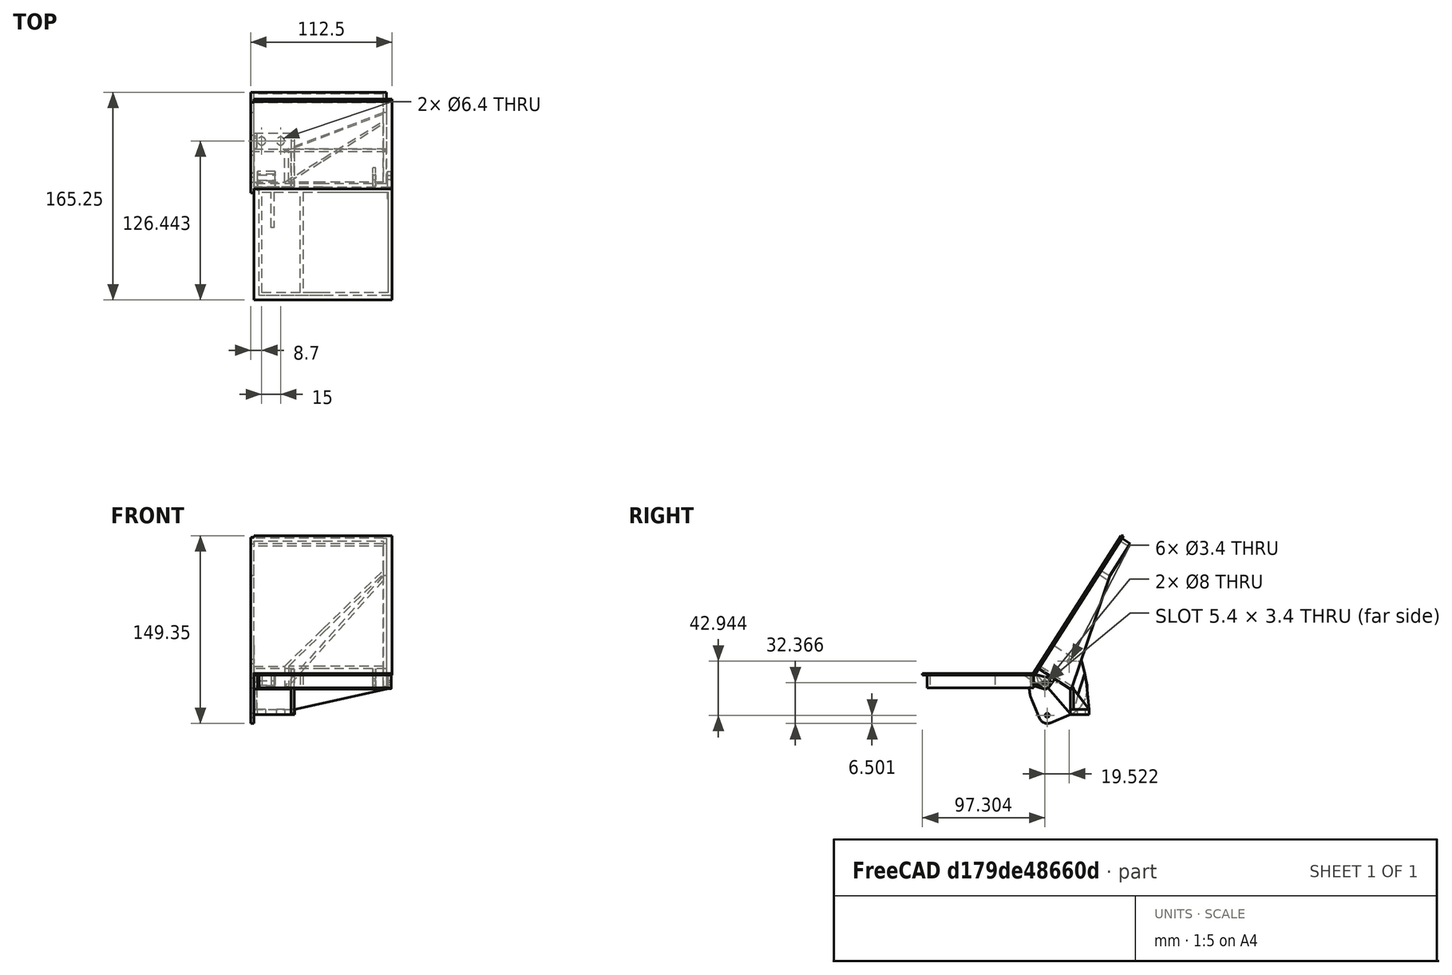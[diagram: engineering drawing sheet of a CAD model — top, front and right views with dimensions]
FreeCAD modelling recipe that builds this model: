
FCSTD DOCUMENT  (FreeCAD 0.19R24291 (Git))
Label: Hopper 6
License: All rights reserved
LicenseURL: http://en.wikipedia.org/wiki/All_rights_reserved
objects: Sketcher::SketchObject×20, PartDesign::Pad×16, PartDesign::Pocket×5, PartDesign::Mirrored×2, PartDesign::Body×2, PartDesign::SubShapeBinder×1, Spreadsheet::Sheet×1
note: 67 computed .brp shape members not serialized (recipe doc carries the construction recipe); baked Part::Feature solids carry a one-line shape summary decoded from their .brp

FEATURE [Sketcher::SketchObject] Sketch
  AttachmentOffset = pos=(0,0,0) rot=(1,0,0;1.00409rad)
  FullyConstrained = true
  MapMode = 5
  Placement = pos=(0,0,0) rot=(1,0,0;1.00409rad)
  Support = -> [XY_Plane]
  expr: .AttachmentOffset.Rotation.Angle = Spreadsheet.BackAngle
  sketch-geometry (4):
    g0: LineSegment StartX=0 StartY=0 StartZ=0 EndX=55 EndY=0 EndZ=0
    g1: LineSegment StartX=55 StartY=0 StartZ=0 EndX=55 EndY=130 EndZ=0
    g2: LineSegment StartX=55 StartY=130 StartZ=0 EndX=0 EndY=130 EndZ=0
    g3: LineSegment StartX=0 StartY=130 StartZ=0 EndX=0 EndY=0 EndZ=0
  constraints (11):
    c: Coincident(g0,g1)
    c: Coincident(g1,g2)
    c: Coincident(g2,g3)
    c: Coincident(g3,g0)
    c: Horizontal(g0)
    c: Horizontal(g2)
    c: Vertical(g1)
    c: Vertical(g3)
    c: Coincident(g0,g-1)
    c: Distance(g1) = 130
    c: Distance(g0) = 55
FEATURE [PartDesign::Pad] Pad
  Direction = (0,-1,0)
  Length = 1.5
  Length2 = 100
  Profile = -> Sketch
  Type = 0
  UseCustomVector = true
FEATURE [PartDesign::Mirrored] Mirrored
  BaseFeature = -> Pad
  MirrorPlane = -> Sketch [V_Axis]
  Originals = -> [Pad]
FEATURE [Sketcher::SketchObject] Sketch001
  FullyConstrained = true
  MapMode = 5
  Placement = pos=(-55,0,0) rot=(0.57735,-0.57735,-0.57735;2.0944rad)
  Support = -> [Mirrored]
  expr: Constraints[34] = 10.33mm
  expr: Constraints[41] = Spreadsheet.BackAngle
  sketch-geometry (23):
    g0: ArcOfCircle CenterX=-24.9137 CenterY=5.10111 CenterZ=0 NormalX=0 NormalY=0 NormalZ=1 AngleXU=0 Radius=12.5 StartAngle=0.484009 EndAngle=3.43434
    g1: ArcOfCircle CenterX=-9.25499 CenterY=-33.1694 CenterZ=0 NormalX=0 NormalY=0 NormalZ=1 AngleXU=0 Radius=6.5 StartAngle=3.35841 EndAngle=6.84312
    g2: Circle CenterX=-7.30441 CenterY=-7.30441 CenterZ=0 NormalX=0 NormalY=0 NormalZ=1 AngleXU=0 Radius=4
    g3: Circle CenterX=-9.25499 CenterY=-33.1694 CenterZ=0 NormalX=0 NormalY=0 NormalZ=1 AngleXU=0 Radius=1.7
    g4: Circle CenterX=-26.826 CenterY=9.77502 CenterZ=0 NormalX=0 NormalY=0 NormalZ=1 AngleXU=0 Radius=1.7
    g5: LineSegment StartX=-9.25499 StartY=-33.1694 StartZ=0 EndX=-18.0405 EndY=-11.6972 EndZ=0
    g6: LineSegment StartX=-18.0405 StartY=-11.6972 StartZ=0 EndX=-26.826 EndY=9.77502 EndZ=0
    g7: LineSegment StartX=-18.0405 StartY=-11.6972 StartZ=0 EndX=-7.30441 EndY=-7.30441 EndZ=0
    g8: GeomPoint X=-29.6472 Y=16.6702 Z=0
    g9: ArcOfCircle CenterX=-18.0405 CenterY=-11.6972 CenterZ=0 NormalX=0 NormalY=0 NormalZ=1 AngleXU=0 Radius=23 StartAngle=2.53079 EndAngle=4.81858
    g10: ArcOfCircle CenterX=-18.0405 CenterY=-11.6972 CenterZ=0 NormalX=0 NormalY=0 NormalZ=1 AngleXU=0 Radius=23 StartAngle=5.38296 EndAngle=7.67074
    g11: LineSegment StartX=-7.30441 StartY=-7.30441 StartZ=0 EndX=-7.30441 EndY=0 EndZ=0
    g12: LineSegment StartX=-7.30441 StartY=-7.30441 StartZ=0 EndX=0 EndY=-7.30441 EndZ=0
    g13: ArcOfCircle CenterX=-18.0405 CenterY=-11.6972 CenterZ=0 NormalX=0 NormalY=0 NormalZ=1 AngleXU=0 Radius=23 StartAngle=5.38296 EndAngle=6.84989
    g14: LineSegment StartX=-28.0362 StartY=46.853 StartZ=0 EndX=1.36396 EndY=0.650563 EndZ=0
    g15: LineSegment StartX=0 StartY=0 StartZ=0 EndX=1.26551 EndY=0.805287 EndZ=0
    g16: LineSegment StartX=1.26551 StartY=0.805287 StartZ=0 EndX=1.36396 EndY=0.650563 EndZ=0
    g17: ArcOfCircle CenterX=-18.0405 CenterY=-11.6972 CenterZ=0 NormalX=0 NormalY=0 NormalZ=1 AngleXU=0 Radius=23 StartAngle=2.91307 EndAngle=4.32118
    g18: ArcOfCircle CenterX=-9.25499 CenterY=-33.1694 CenterZ=0 NormalX=0 NormalY=0 NormalZ=1 AngleXU=0 Radius=6.5 StartAngle=4.32118 EndAngle=5.88035
    g19: ArcOfCircle CenterX=-18.0405 CenterY=-11.6972 CenterZ=0 NormalX=0 NormalY=0 NormalZ=1 AngleXU=0 Radius=23 StartAngle=5.88035 EndAngle=6.84989
    g20: LineSegment StartX=-11.7335 StartY=-39.1783 StartZ=0 EndX=-26.8105 EndY=-32.9595 EndZ=0
    g21: LineSegment StartX=-3.2753 StartY=-35.7176 StartZ=0 EndX=3.11842 EndY=-20.7138 EndZ=0
    g22: LineSegment StartX=-40.4425 StartY=-6.48667 StartZ=0 EndX=-28.0362 EndY=46.853 EndZ=0
  constraints (66):
    c: Coincident(g3,g1)
    c: Coincident(g5,g1)
    c: Coincident(g6,g5)
    c: Coincident(g6,g4)
    c: Coincident(g7,g5)
    c: Coincident(g7,g2)
    c: Distance(g7) = 11.6
    c: Distance(g1,g4) = 46.4
    c: Perpendicular(g6,g7)
    c: Perpendicular(g5,g7)
    c: PointOnObject(g0,g6)
    c: Diameter(g0) = 25
    c: PointOnObject(g8,g0)
    c: PointOnObject(g8,g6)
    c: Distance(g4,g8) = 7.45
    c: Equal(g6,g5)
    c: Diameter(g1) = 13
    c: Coincident(g9,g5)
    c: Coincident(g9,g0)
    c: Coincident(g10,g9)
    c: Coincident(g10,g0)
    c: Equal(g9,g10)
    c: Diameter(g10) = 46
    c: Coincident(g9,g1)
    c: Diameter(g2) = 8
    c: Diameter(g3) = 3.4
    c: Equal(g3,g4)
    c: Coincident(g11,g2)
    c: PointOnObject(g11,g-1)
    c: Vertical(g11)
    c: Coincident(g12,g2)
    c: PointOnObject(g12,g-2)
    c: Horizontal(g12)
    c: Equal(g12,g11)
    c: Distance(g2,g-1) = 10.33
    c: Distance(g12) = 7.30441
    c: Coincident(g10,g1)
    c: Coincident(g13,g9)
    c: Coincident(g13,g1)
    c: Coincident(g14,g13)
    c: Tangent(g14,g10)
    c: Angle(g14,g-1) = 1.00409
    c: Coincident(g15,g-1)
    c: Distance(g15) = 1.5
    c: Coincident(g16,g15)
    c: Perpendicular(g15,g16)
    c: Coincident(g13,g16)
    c: Coincident(g17,g5)
    c: PointOnObject(g17,g9)
    c: Coincident(g18,g3)
    c: PointOnObject(g18,g1)
    c: Coincident(g19,g17)
    c: Coincident(g19,g14)
    c: Coincident(g20,g18)
    c: Coincident(g20,g17)
    c: Coincident(g21,g18)
    c: Coincident(g21,g19)
    c: Tangent(g17,g20)
    c: Tangent(g20,g18)
    c: Tangent(g18,g21)
    c: Tangent(g21,g19)
    c: Coincident(g22,g17)
    c: Coincident(g22,g14)
    c: Tangent(g22,g17)
    c: Tangent(g22,g0)
    c: Perpendicular(g14,g15)
FEATURE [PartDesign::Pad] Pad001
  BaseFeature = -> Mirrored
  Direction = (1,1,1)
  Length = 1.5
  Length2 = 100
  Profile = -> Sketch001
  Type = 0
FEATURE [Sketcher::SketchObject] Sketch002
  FullyConstrained = false
  MapMode = 5
  Placement = pos=(0,-9e-15,5.7e-15) rot=(0,0.876601,0.481218;3.14159rad)
  Support = -> [Pad001]
  sketch-geometry (13):
    g0: LineSegment StartX=-50.3995 StartY=127.591 StartZ=0 EndX=-50.3995 EndY=4.62451 EndZ=0
    g1: LineSegment StartX=55.0842 StartY=7.02451 StartZ=0 EndX=30.5525 EndY=7.02451 EndZ=0
    g2: LineSegment StartX=30.5525 StartY=7.02451 StartZ=0 EndX=-47.9995 EndY=97.2605 EndZ=0
    g3: LineSegment StartX=-47.9995 StartY=97.2605 StartZ=0 EndX=-47.9995 EndY=127.591 EndZ=0
    g4: LineSegment StartX=-47.9995 StartY=127.591 StartZ=0 EndX=-50.3995 EndY=127.591 EndZ=0
    g5: LineSegment StartX=-50.3995 StartY=4.62451 StartZ=0 EndX=55.0842 EndY=4.62451 EndZ=0
    g6: LineSegment StartX=55.0842 StartY=4.62451 StartZ=0 EndX=55.0842 EndY=7.02451 EndZ=0
    g7: LineSegment StartX=27.3705 StartY=7.02451 StartZ=0 EndX=-47.9995 EndY=93.6052 EndZ=0
    g8: LineSegment StartX=-47.9995 StartY=93.6052 StartZ=0 EndX=-47.9995 EndY=7.02451 EndZ=0
    g9: LineSegment StartX=-47.9995 StartY=7.02451 StartZ=0 EndX=27.3705 EndY=7.02451 EndZ=0
    g10: LineSegment StartX=27.3705 StartY=7.02451 StartZ=0 EndX=27.3705 EndY=4.62451 EndZ=0
    g11: LineSegment StartX=-47.9995 StartY=93.6052 StartZ=0 EndX=-50.3995 EndY=93.6052 EndZ=0
    g12: LineSegment StartX=-27.7414 StartY=70.3339 StartZ=0 EndX=-25.9312 EndY=71.9097 EndZ=0
  constraints (37):
    c: Vertical(g0)
    c: Horizontal(g1)
    c: Coincident(g1,g2)
    c: Coincident(g2,g3)
    c: Coincident(g3,g4)
    c: Horizontal(g4)
    c: Horizontal(g5)
    c: Coincident(g5,g6)
    c: Coincident(g6,g1)
    c: Coincident(g7,g8)
    c: Vertical(g8)
    c: Coincident(g8,g9)
    c: Coincident(g9,g7)
    c: Horizontal(g9)
    c: Vertical(g6)
    c: Distance(g6) = 2.4
    c: Coincident(g10,g7)
    c: PointOnObject(g10,g5)
    c: Vertical(g10)
    c: Coincident(g11,g7)
    c: Horizontal(g11)
    c: Equal(g6,g10)
    c: Equal(g11,g4)
    c: Parallel(g7,g2)
    c: Coincident(g0,g5)
    c: Coincident(g0,g4)
    c: Vertical(g3)
    c: PointOnObject(g11,g0)
    c: Equal(g4,g6)
    c: PointOnObject(g12,g7)
    c: PointOnObject(g12,g2)
    c: Perpendicular(g2,g12)
    c: Equal(g6,g12)
    c: DistanceX(g7) = -47.9995
    c: DistanceY(g7) = 93.6052
    c: DistanceX(g5) = 55.0842
    c: DistanceY(g5) = 4.62451
FEATURE [PartDesign::Pad] Pad002
  BaseFeature = -> Pad001
  Direction = (1,1,1)
  Length = 30
  Length2 = 100
  Profile = -> Sketch002
  Type = 0
FEATURE [Sketcher::SketchObject] Sketch003
  FullyConstrained = true
  MapMode = 5
  Placement = pos=(-56.5,0,0) rot=(0.57735,-0.57735,-0.57735;2.0944rad)
  Support = -> [Pad002]
  expr: Constraints[6] = Sketch001.Constraints[6]
  expr: Constraints[7] = Sketch001.Constraints[7]
  expr: Constraints[11] = Sketch001.Constraints[11]
  expr: Constraints[14] = Sketch001.Constraints[14]
  expr: Constraints[22] = Sketch001.Constraints[22]
  expr: Constraints[41] = Sketch001.Constraints[41]
  expr: Constraints[16] = Sketch001.Constraints[16]
  expr: Constraints[44] = Sketch001.Constraints[44]
  expr: Constraints[24] = Sketch001.Constraints[24]
  expr: Constraints[25] = Sketch001.Constraints[25]
  expr: Constraints[34] = Sketch001.Constraints[34]
  expr: Constraints[43] = Sketch001.Constraints[43]
  sketch-geometry (31):
    g0: ArcOfCircle CenterX=-25.2764 CenterY=4.56949 CenterZ=0 NormalX=0 NormalY=0 NormalZ=1 AngleXU=0 Radius=12.5 StartAngle=0.51389 EndAngle=3.46422
    g1: ArcOfCircle CenterX=-8.48139 CenterY=-33.2161 CenterZ=0 NormalX=0 NormalY=0 NormalZ=1 AngleXU=0 Radius=6.5 StartAngle=3.38829 EndAngle=6.873
    g2: Circle CenterX=-7.30441 CenterY=-7.30441 CenterZ=0 NormalX=0 NormalY=0 NormalZ=1 AngleXU=0 Radius=4
    g3: Circle CenterX=-8.48139 CenterY=-33.2161 CenterZ=0 NormalX=0 NormalY=0 NormalZ=1 AngleXU=0 Radius=1.7
    g4: Circle CenterX=-27.3276 CenterY=9.18417 CenterZ=0 NormalX=0 NormalY=0 NormalZ=1 AngleXU=0 Radius=1.7
    g5: LineSegment StartX=-8.48139 StartY=-33.2161 StartZ=0 EndX=-17.9045 EndY=-12.016 EndZ=0
    g6: LineSegment StartX=-17.9045 StartY=-12.016 StartZ=0 EndX=-27.3276 EndY=9.18417 EndZ=0
    g7: LineSegment StartX=-17.9045 StartY=-12.016 StartZ=0 EndX=-7.30441 EndY=-7.30441 EndZ=0
    g8: GeomPoint X=-30.3535 Y=15.992 Z=0
    g9: ArcOfCircle CenterX=-17.9045 CenterY=-12.016 CenterZ=0 NormalX=0 NormalY=0 NormalZ=1 AngleXU=0 Radius=23 StartAngle=2.56067 EndAngle=4.84846
    g10: ArcOfCircle CenterX=-17.9045 CenterY=-12.016 CenterZ=0 NormalX=0 NormalY=0 NormalZ=1 AngleXU=0 Radius=23 StartAngle=5.41284 EndAngle=7.70062
    g11: LineSegment StartX=-7.30441 StartY=-7.30441 StartZ=0 EndX=-7.30441 EndY=0 EndZ=0
    g12: LineSegment StartX=-7.30441 StartY=-7.30441 StartZ=0 EndX=0 EndY=-7.30441 EndZ=0
    g13: ArcOfCircle CenterX=-17.9045 CenterY=-12.016 CenterZ=0 NormalX=0 NormalY=0 NormalZ=1 AngleXU=0 Radius=23 StartAngle=5.41284 EndAngle=6.84989
    g14: LineSegment StartX=-29.176 StartY=48.5391 StartZ=0 EndX=1.5 EndY=0.331766 EndZ=0
    g15: LineSegment StartX=0 StartY=0 StartZ=0 EndX=1.5 EndY=0 EndZ=0
    g16: LineSegment StartX=1.5 StartY=0 StartZ=0 EndX=1.5 EndY=0.331766 EndZ=0
    g17: ArcOfCircle CenterX=-17.9045 CenterY=-12.016 CenterZ=0 NormalX=0 NormalY=0 NormalZ=1 AngleXU=0 Radius=23 StartAngle=2.94295 EndAngle=4.35106
    g18: ArcOfCircle CenterX=-8.48139 CenterY=-33.2161 CenterZ=0 NormalX=0 NormalY=0 NormalZ=1 AngleXU=0 Radius=6.5 StartAngle=4.35106 EndAngle=5.91023
    g19: ArcOfCircle CenterX=-17.9045 CenterY=-12.016 CenterZ=0 NormalX=0 NormalY=0 NormalZ=1 AngleXU=0 Radius=23 StartAngle=5.91023 EndAngle=6.84989
    g20: LineSegment StartX=-10.7792 StartY=-39.2964 StartZ=0 EndX=-26.0353 EndY=-33.5308 EndZ=0
    g21: LineSegment StartX=-2.42824 StartY=-35.5845 StartZ=0 EndX=3.51436 EndY=-20.3965 EndZ=0
    g22: LineSegment StartX=-40.4522 StartY=-7.47706 StartZ=0 EndX=-29.176 EndY=48.5391 EndZ=0
    g23: ArcOfCircle CenterX=-17.9045 CenterY=-12.016 CenterZ=0 NormalX=0 NormalY=0 NormalZ=1 AngleXU=0 Radius=22.2 StartAngle=5.41284 EndAngle=7.70062
    g24: ArcOfCircle CenterX=-17.9045 CenterY=-12.016 CenterZ=0 NormalX=0 NormalY=0 NormalZ=1 AngleXU=0 Radius=22.2 StartAngle=2.56067 EndAngle=4.84846
    g25: ArcOfCircle CenterX=-3.07962 CenterY=-29.6007 CenterZ=0 NormalX=0 NormalY=0 NormalZ=1 AngleXU=0 Radius=0.8 StartAngle=2.27123 EndAngle=3.73142
    g26: ArcOfCircle CenterX=-14.7846 CenterY=-34.8034 CenterZ=0 NormalX=0 NormalY=0 NormalZ=1 AngleXU=0 Radius=0.8 StartAngle=0.246691 EndAngle=1.70686
    g27: ArcOfCircle CenterX=-8.48139 CenterY=-33.2161 CenterZ=0 NormalX=0 NormalY=0 NormalZ=1 AngleXU=0 Radius=5.7 StartAngle=3.38829 EndAngle=6.873
    g28: ArcOfCircle CenterX=-37.1315 CenterY=0.606294 CenterZ=0 NormalX=0 NormalY=0 NormalZ=1 AngleXU=0 Radius=0.8 StartAngle=5.70226 EndAngle=6.60581
    g29: ArcOfCircle CenterX=-14.3909 CenterY=10.7141 CenterZ=0 NormalX=0 NormalY=0 NormalZ=1 AngleXU=0 Radius=0.8 StartAngle=3.65547 EndAngle=4.55903
    g30: ArcOfCircle CenterX=-25.2764 CenterY=4.56949 CenterZ=0 NormalX=0 NormalY=0 NormalZ=1 AngleXU=0 Radius=11.7 StartAngle=0.51389 EndAngle=3.46422
  constraints (90):
    c: Coincident(g3,g1)
    c: Coincident(g5,g1)
    c: Coincident(g6,g5)
    c: Coincident(g6,g4)
    c: Coincident(g7,g5)
    c: Coincident(g7,g2)
    c: Distance(g7) = 11.6
    c: Distance(g1,g4) = 46.4
    c: Perpendicular(g6,g7)
    c: Perpendicular(g5,g7)
    c: PointOnObject(g0,g6)
    c: Diameter(g0) = 25
    c: PointOnObject(g8,g0)
    c: PointOnObject(g8,g6)
    c: Distance(g4,g8) = 7.45
    c: Equal(g6,g5)
    c: Diameter(g1) = 13
    c: Coincident(g9,g5)
    c: Coincident(g9,g0)
    c: Coincident(g10,g9)
    c: Coincident(g10,g0)
    c: Equal(g9,g10)
    c: Diameter(g10) = 46
    c: Coincident(g9,g1)
    c: Diameter(g2) = 8
    c: Diameter(g3) = 3.4
    c: Equal(g3,g4)
    c: Coincident(g11,g2)
    c: PointOnObject(g11,g-1)
    c: Vertical(g11)
    c: Coincident(g12,g2)
    c: PointOnObject(g12,g-2)
    c: Horizontal(g12)
    c: Equal(g12,g11)
    c: Distance(g2,g-1) = 10.33
    c: Distance(g12) = 7.30441
    c: Coincident(g10,g1)
    c: Coincident(g13,g9)
    c: Coincident(g13,g1)
    c: Coincident(g14,g13)
    c: Tangent(g14,g10)
    c: Angle(g14,g-1) = 1.00409
    c: Coincident(g15,g-1)
    c: Distance(g15) = 1.5
    c: Angle(g-1,g15) = 0
    c: Coincident(g16,g15)
    c: Perpendicular(g15,g16)
    c: Coincident(g13,g16)
    c: Coincident(g17,g5)
    c: PointOnObject(g17,g9)
    c: Coincident(g18,g3)
    c: PointOnObject(g18,g1)
    c: Coincident(g19,g17)
    c: Coincident(g19,g14)
    c: Coincident(g20,g18)
    c: Coincident(g20,g17)
    c: Coincident(g21,g18)
    c: Coincident(g21,g19)
    c: Tangent(g17,g20)
    c: Tangent(g20,g18)
    c: Tangent(g18,g21)
    c: Tangent(g21,g19)
    c: Coincident(g22,g17)
    c: Coincident(g22,g14)
    c: Tangent(g22,g17)
    c: Tangent(g22,g0)
    c: Coincident(g23,g9)
    c: Coincident(g24,g9)
    c: Coincident(g25,g1)
    c: Coincident(g25,g23)
    c: Coincident(g26,g1)
    c: Coincident(g26,g24)
    c: Coincident(g27,g1)
    c: Coincident(g27,g26)
    c: Coincident(g27,g25)
    c: Coincident(g28,g0)
    c: Coincident(g28,g24)
    c: Coincident(g29,g0)
    c: Coincident(g29,g23)
    c: Coincident(g30,g0)
    c: Coincident(g30,g29)
    c: Coincident(g30,g28)
    c: Tangent(g23,g29)
    c: Tangent(g29,g30)
    c: Tangent(g28,g24)
    c: Tangent(g28,g30)
    c: Tangent(g24,g26)
    c: Tangent(g26,g27)
    c: Tangent(g27,g25)
    c: Diameter(g25) = 1.6
FEATURE [PartDesign::SubShapeBinder] Binder
  BindMode = 0
  ClaimChildren = false
  Context = -> Body001 [Binder.]
  Fuse = false
  MakeFace = true
  PartialLoad = false
  Relative = true
  Support = -> [Body[Pad002.Face6]]
  _Version = 2
FEATURE [Sketcher::SketchObject] Sketch004
  FullyConstrained = true
  MapMode = 5
  Support = -> [XY_Plane001]
  sketch-geometry (4):
    g0: LineSegment StartX=0 StartY=0 StartZ=0 EndX=55 EndY=0 EndZ=0
    g1: LineSegment StartX=55 StartY=0 StartZ=0 EndX=55 EndY=-90 EndZ=0
    g2: LineSegment StartX=55 StartY=-90 StartZ=0 EndX=0 EndY=-90 EndZ=0
    g3: LineSegment StartX=0 StartY=-90 StartZ=0 EndX=0 EndY=0 EndZ=0
  constraints (11):
    c: Coincident(g0,g1)
    c: Coincident(g1,g2)
    c: Coincident(g2,g3)
    c: Coincident(g3,g0)
    c: Horizontal(g0)
    c: Horizontal(g2)
    c: Vertical(g1)
    c: Vertical(g3)
    c: Coincident(g0,g-1)
    c: Distance(g2) = 55
    c: Distance(g1) = 90
FEATURE [PartDesign::Pad] Pad003
  Direction = (1,1,1)
  Length = 1.28
  Length2 = 100
  Profile = -> Sketch004
  Reversed = true
  Type = 0
FEATURE [PartDesign::Mirrored] Mirrored001
  BaseFeature = -> Pad003
  MirrorPlane = -> Sketch004 [V_Axis]
  Originals = -> [Pad003]
FEATURE [Sketcher::SketchObject] Sketch005
  AttachmentOffset = pos=(0,0,-52) rot=(0,0,1;0rad)
  FullyConstrained = false
  MapMode = 5
  Placement = pos=(-52,1.15e-14,-1.15e-14) rot=(0.57735,0.57735,0.57735;2.0944rad)
  Support = -> [YZ_Plane001]
  sketch-geometry (12):
    g0: Circle CenterX=7.30441 CenterY=-7.30441 CenterZ=0 NormalX=0 NormalY=0 NormalZ=1 AngleXU=0 Radius=4
    g1: LineSegment StartX=7.30441 StartY=-7.30441 StartZ=0 EndX=0 EndY=-7.30441 EndZ=0
    g2: LineSegment StartX=7.30441 StartY=-7.30441 StartZ=0 EndX=7.30441 EndY=0 EndZ=0
    g3: LineSegment StartX=5.2068 StartY=-9.00441 StartZ=0 EndX=9.40203 EndY=-9.00441 EndZ=0
    g4: LineSegment StartX=5.2068 StartY=-5.60441 StartZ=0 EndX=9.40203 EndY=-5.60441 EndZ=0
    g5: ArcOfCircle CenterX=7.30441 CenterY=-7.30441 CenterZ=0 NormalX=0 NormalY=0 NormalZ=1 AngleXU=0 Radius=2.7 StartAngle=2.46052 EndAngle=3.82267
    g6: ArcOfCircle CenterX=7.30441 CenterY=-7.30441 CenterZ=0 NormalX=0 NormalY=0 NormalZ=1 AngleXU=0 Radius=2.7 StartAngle=5.60211 EndAngle=6.96426
    g7: ArcOfCircle CenterX=7.30441 CenterY=-7.30441 CenterZ=0 NormalX=0 NormalY=0 NormalZ=1 AngleXU=0 Radius=5 StartAngle=4.40509 EndAngle=7.57383
    g8: LineSegment StartX=0 StartY=0 StartZ=0 EndX=8.68691 EndY=-2.49934 EndZ=0
    g9: LineSegment StartX=5.792 StartY=-12.0702 StartZ=0 EndX=-3 EndY=-9.28 EndZ=0
    g10: LineSegment StartX=0 StartY=0 StartZ=0 EndX=-3 EndY=0 EndZ=0
    g11: LineSegment StartX=-3 StartY=0 StartZ=0 EndX=-3 EndY=-9.28 EndZ=0
  constraints (34):
    c: Coincident(g1,g0)
    c: PointOnObject(g1,g-2)
    c: Coincident(g2,g0)
    c: PointOnObject(g2,g-1)
    c: Vertical(g2)
    c: Horizontal(g1)
    c: Equal(g1,g2)
    c: Distance(g0,g-1) = 10.33
    c: Coincident(g5,g0)
    c: Coincident(g5,g3)
    c: Coincident(g5,g4)
    c: Coincident(g6,g5)
    c: Coincident(g6,g3)
    c: Coincident(g6,g4)
    c: Equal(g6,g5)
    c: Equal(g4,g3)
    c: Distance(g4,g3) = 3.4
    c: Diameter(g5) = 5.4
    c: Coincident(g7,g5)
    c: Coincident(g8,g-1)
    c: Coincident(g8,g7)
    c: Coincident(g9,g7)
    c: Coincident(g10,g8)
    c: PointOnObject(g10,g-1)
    c: Coincident(g11,g10)
    c: Coincident(g11,g9)
    c: Vertical(g11)
    c: Distance(g11) = 9.28
    c: Distance(g10) = 3
    c: Diameter(g7) = 10
    c: Tangent(g8,g7)
    c: Tangent(g7,g9)
    c: Horizontal(g3)
    c: Horizontal(g4)
FEATURE [PartDesign::Pad] Pad004
  BaseFeature = -> Mirrored001
  Direction = (1,1,1)
  Length = 14
  Length2 = 100
  Profile = -> Sketch005
  Type = 0
FEATURE [Sketcher::SketchObject] Sketch006
  FullyConstrained = false
  MapMode = 5
  Placement = pos=(0,0,-1.28) rot=(1,0,0;3.14159rad)
  Support = -> [Pad004]
  sketch-geometry (20):
    g0: LineSegment StartX=-48.4803 StartY=4.08194 StartZ=0 EndX=-41.4307 EndY=4.08194 EndZ=0
    g1: LineSegment StartX=51.8136 StartY=4.08194 StartZ=0 EndX=51.8136 EndY=84.0949 EndZ=0
    g2: LineSegment StartX=51.8136 StartY=84.0949 StartZ=0 EndX=-15.8068 EndY=84.0949 EndZ=0
    g3: LineSegment StartX=-48.4803 StartY=84.0949 StartZ=0 EndX=-48.4803 EndY=4.08194 EndZ=0
    g4: LineSegment StartX=-50.8803 StartY=1.68194 StartZ=0 EndX=54.2136 EndY=1.68194 EndZ=0
    g5: LineSegment StartX=54.2136 StartY=1.68194 StartZ=0 EndX=54.2136 EndY=86.4949 EndZ=0
    g6: LineSegment StartX=54.2136 StartY=86.4949 StartZ=0 EndX=-50.8803 EndY=86.4949 EndZ=0
    g7: LineSegment StartX=-50.8803 StartY=86.4949 StartZ=0 EndX=-50.8803 EndY=1.68194 EndZ=0
    g8: LineSegment StartX=-48.4803 StartY=84.0949 StartZ=0 EndX=-50.8803 EndY=84.0949 EndZ=0
    g9: LineSegment StartX=-48.4803 StartY=84.0949 StartZ=0 EndX=-48.4803 EndY=86.4949 EndZ=0
    g10: LineSegment StartX=51.8136 StartY=4.08194 StartZ=0 EndX=51.8136 EndY=1.68194 EndZ=0
    g11: LineSegment StartX=51.8136 StartY=4.08194 StartZ=0 EndX=54.2136 EndY=4.08194 EndZ=0
    g12: LineSegment StartX=-39.0307 StartY=4.08194 StartZ=0 EndX=-39.0307 EndY=32.4068 EndZ=0
    g13: LineSegment StartX=-39.0307 StartY=32.4068 StartZ=0 EndX=-41.4307 EndY=32.4068 EndZ=0
    g14: LineSegment StartX=-41.4307 StartY=32.4068 StartZ=0 EndX=-41.4307 EndY=4.08194 EndZ=0
    g15: LineSegment StartX=-15.8068 StartY=4.08194 StartZ=0 EndX=-15.8068 EndY=84.0949 EndZ=0
    g16: LineSegment StartX=-18.2068 StartY=84.0949 StartZ=0 EndX=-18.2068 EndY=4.08194 EndZ=0
    g17: LineSegment StartX=-15.8068 StartY=4.08194 StartZ=0 EndX=51.8136 EndY=4.08194 EndZ=0
    g18: LineSegment StartX=-39.0307 StartY=4.08194 StartZ=0 EndX=-18.2068 EndY=4.08194 EndZ=0
    g19: LineSegment StartX=-18.2068 StartY=84.0949 StartZ=0 EndX=-48.4803 EndY=84.0949 EndZ=0
  constraints (48):
    c: Coincident(g17,g1)
    c: Coincident(g1,g2)
    c: Coincident(g19,g3)
    c: Coincident(g3,g0)
    c: Horizontal(g0)
    c: Horizontal(g2)
    c: Vertical(g1)
    c: Vertical(g3)
    c: Coincident(g4,g5)
    c: Coincident(g5,g6)
    c: Coincident(g6,g7)
    c: Coincident(g7,g4)
    c: Horizontal(g4)
    c: Horizontal(g6)
    c: Vertical(g5)
    c: Vertical(g7)
    c: Coincident(g8,g19)
    c: PointOnObject(g8,g7)
    c: Horizontal(g8)
    c: Coincident(g9,g19)
    c: PointOnObject(g9,g6)
    c: Vertical(g9)
    c: Coincident(g10,g17)
    c: PointOnObject(g10,g4)
    c: Vertical(g10)
    c: Coincident(g11,g17)
    c: PointOnObject(g11,g5)
    c: Horizontal(g11)
    c: Equal(g10,g11)
    c: Equal(g11,g8)
    c: Equal(g8,g9)
    c: Distance(g9) = 2.4
    c: Coincident(g12,g13)
    c: Coincident(g13,g14)
    c: Horizontal(g13)
    c: Vertical(g12)
    c: Vertical(g14)
    c: Vertical(g15)
    c: Vertical(g16)
    c: Tangent(g0,g17)
    c: Tangent(g0,g18)
    c: Coincident(g15,g17)
    c: Coincident(g18,g16)
    c: Coincident(g12,g18)
    c: Coincident(g0,g14)
    c: Coincident(g2,g15)
    c: Coincident(g19,g16)
    c: Tangent(g2,g19)
FEATURE [PartDesign::Pad] Pad005
  BaseFeature = -> Pad004
  Direction = (1,1,1)
  Length = 10
  Length2 = 100
  Profile = -> Sketch006
  Type = 0
FEATURE [Sketcher::SketchObject] Sketch007
  ExternalGeometry = -> [Pad002]
  FullyConstrained = true
  MapMode = 5
  Placement = pos=(-55,0,0) rot=(0.57735,0.57735,0.57735;2.0944rad)
  Support = -> [Pad002]
  sketch-geometry (7):
    g0: LineSegment StartX=27.7929 StartY=-12.2042 StartZ=0 EndX=29.0813 EndY=-10.1793 EndZ=0
    g1: LineSegment StartX=27.7929 StartY=-12.2042 StartZ=0 EndX=27.7929 EndY=-32.5242 EndZ=0
    g2: LineSegment StartX=30.1929 StartY=-12.2042 StartZ=0 EndX=30.1929 EndY=-28.3642 EndZ=0
    g3: LineSegment StartX=42.6929 StartY=-28.3642 StartZ=0 EndX=42.6929 EndY=-32.5242 EndZ=0
    g4: LineSegment StartX=42.6929 StartY=-32.5242 StartZ=0 EndX=27.7929 EndY=-32.5242 EndZ=0
    g5: LineSegment StartX=30.1929 StartY=-28.3642 StartZ=0 EndX=42.6929 EndY=-28.3642 EndZ=0
    g6: ArcOfCircle CenterX=27.7929 CenterY=-12.2042 CenterZ=0 NormalX=0 NormalY=0 NormalZ=1 AngleXU=0 Radius=2.4 StartAngle=6.37745e-08 EndAngle=1.00409
  constraints (19):
    c: Vertical(g1)
    c: Vertical(g2)
    c: Coincident(g5,g3)
    c: Coincident(g3,g4)
    c: Horizontal(g4)
    c: Vertical(g3)
    c: Distance(g3) = 4.16
    c: Coincident(g5,g2)
    c: Coincident(g0,g-3)
    c: Coincident(g0,g-3)
    c: Coincident(g1,g0)
    c: Coincident(g6,g0)
    c: Coincident(g6,g2)
    c: Coincident(g6,g0)
    c: Tangent(g2,g6)
    c: Distance(g5) = 12.5
    c: Coincident(g4,g1)
    c: Horizontal(g5)
    c: Distance(g1) = 20.32
FEATURE [PartDesign::Pad] Pad006
  BaseFeature = -> Pad002
  Direction = (1,1,1)
  Length = 27.4
  Length2 = 100
  Profile = -> Sketch007
  Type = 0
FEATURE [Sketcher::SketchObject] Sketch008
  ExternalGeometry = -> [Pad006]
  FullyConstrained = false
  MapMode = 5
  Placement = pos=(0,0,-28.3642) rot=(0,0,1;0rad)
  Support = -> [Pad006]
  sketch-geometry (5):
    g0: Circle CenterX=-48.8 CenterY=-36.4929 CenterZ=0 NormalX=0 NormalY=0 NormalZ=1 AngleXU=0 Radius=3.2
    g1: Circle CenterX=-48.8 CenterY=-21.4929 CenterZ=0 NormalX=0 NormalY=0 NormalZ=1 AngleXU=0 Radius=3.2
    g2: LineSegment StartX=-42.6 StartY=-42.6929 StartZ=0 EndX=-48.8 EndY=-36.4929 EndZ=0
    g3: LineSegment StartX=-48.8 StartY=-21.4929 StartZ=0 EndX=-55 EndY=-15.2929 EndZ=0
    g4: LineSegment StartX=-48.8 StartY=-21.4929 StartZ=0 EndX=-42.6 EndY=-15.2929 EndZ=0
  constraints (9):
    c: Vertical(g0,g1)
    c: Diameter(g0) = 6.4
    c: Equal(g0,g1)
    c: Coincident(g2,g0)
    c: Distance(g0,g1) = 15
    c: Coincident(g3,g1)
    c: Coincident(g4,g1)
    c: Equal(g3,g4)
    c: Equal(g4,g2)
FEATURE [Spreadsheet::Sheet] Spreadsheet
  cells = B1=-; B2(BackAngle)=57.53
FEATURE [Sketcher::SketchObject] Sketch010
  AttachmentOffset = pos=(0,0,42) rot=(0,0,1;0rad)
  FullyConstrained = false
  MapMode = 5
  Placement = pos=(42,-9.3e-15,9.3e-15) rot=(0.57735,0.57735,0.57735;2.0944rad)
  Support = -> [YZ_Plane]
  sketch-geometry (7):
    g0: Circle CenterX=7.30441 CenterY=-7.30441 CenterZ=0 NormalX=0 NormalY=0 NormalZ=1 AngleXU=0 Radius=1.7
    g1: ArcOfCircle CenterX=7.30441 CenterY=-7.30441 CenterZ=0 NormalX=0 NormalY=0 NormalZ=1 AngleXU=0 Radius=4.7 StartAngle=3.43474 EndAngle=5.65843
    g2: LineSegment StartX=2.80492 StartY=-8.66255 StartZ=0 EndX=-0.13424 EndY=1.07476 EndZ=0
    g3: LineSegment StartX=11.1166 StartY=-10.0534 StartZ=0 EndX=15.4129 EndY=-4.09557 EndZ=0
    g4: LineSegment StartX=-0.13424 StartY=1.07476 StartZ=0 EndX=2.39721 EndY=4.52212 EndZ=0
    g5: LineSegment StartX=2.39721 StartY=4.52212 StartZ=0 EndX=15.4129 EndY=-4.09557 EndZ=0
    g6: LineSegment StartX=11.1166 StartY=-10.0534 StartZ=0 EndX=8.68329 EndY=-8.29874 EndZ=0
  constraints (15):
    c: DistanceX(g0) = 7.30441
    c: DistanceY(g0) = -7.30441
    c: Coincident(g1,g0)
    c: Coincident(g2,g1)
    c: Coincident(g3,g1)
    c: Tangent(g3,g1)
    c: Tangent(g1,g2)
    c: Coincident(g4,g2)
    c: Coincident(g5,g4)
    c: Coincident(g5,g3)
    c: Diameter(g0) = 3.4
    c: Coincident(g6,g1)
    c: PointOnObject(g6,g0)
    c: PointOnObject(g0,g6)
    c: Distance(g6) = 3
FEATURE [Sketcher::SketchObject] Sketch011
  AttachmentOffset = pos=(0,0,51) rot=(0,0,1;0rad)
  FullyConstrained = false
  MapMode = 5
  Placement = pos=(51,-1.13e-14,1.13e-14) rot=(0.57735,0.57735,0.57735;2.0944rad)
  Support = -> [YZ_Plane001]
  sketch-geometry (5):
    g0: Circle CenterX=7.30441 CenterY=-7.30441 CenterZ=0 NormalX=0 NormalY=0 NormalZ=1 AngleXU=0 Radius=1.7
    g1: ArcOfCircle CenterX=7.30441 CenterY=-7.30441 CenterZ=0 NormalX=0 NormalY=0 NormalZ=1 AngleXU=0 Radius=4.7 StartAngle=4.10616 EndAngle=7.64674
    g2: LineSegment StartX=4.62648 StartY=-11.1669 StartZ=0 EndX=-10.0869 EndY=-0.965795 EndZ=0
    g3: LineSegment StartX=8.2715 StartY=-2.70498 StartZ=0 EndX=0 EndY=-0.965795 EndZ=0
    g4: LineSegment StartX=0 StartY=-0.965795 StartZ=0 EndX=-10.0869 EndY=-0.965795 EndZ=0
  constraints (13):
    c: DistanceX(g0) = 7.30441
    c: DistanceY(g0) = -7.30441
    c: Diameter(g0) = 3.4
    c: Coincident(g1,g0)
    c: Coincident(g2,g1)
    c: Coincident(g3,g1)
    c: Coincident(g4,g3)
    c: Coincident(g4,g2)
    c: Tangent(g1,g3)
    c: Tangent(g2,g1)
    c: Diameter(g1) = 9.4
    c: Horizontal(g4)
    c: PointOnObject(g3,g-2)
FEATURE [PartDesign::Pad] Pad009
  BaseFeature = -> Pad005
  Direction = (1,1,1)
  Length = 3.2
  Length2 = 100
  Profile = -> Sketch011
  Type = 0
FEATURE [Sketcher::SketchObject] Sketch012
  ExternalGeometry = -> [Pad006]
  FullyConstrained = true
  MapMode = 5
  Placement = pos=(0,0,-28.3642) rot=(0,0,1;0rad)
  Support = -> [Pad006]
  sketch-geometry (6):
    g0: Circle CenterX=-48.8 CenterY=36.4429 CenterZ=0 NormalX=0 NormalY=0 NormalZ=1 AngleXU=0 Radius=3.2
    g1: Circle CenterX=-33.8 CenterY=36.4429 CenterZ=0 NormalX=0 NormalY=0 NormalZ=1 AngleXU=0 Radius=3.2
    g2: LineSegment StartX=-55 StartY=42.6929 StartZ=0 EndX=-48.8 EndY=36.4429 EndZ=0
    g3: LineSegment StartX=-48.8 StartY=36.4429 StartZ=0 EndX=-55 EndY=30.1929 EndZ=0
    g4: LineSegment StartX=-33.8 StartY=36.4429 StartZ=0 EndX=-27.6 EndY=42.6929 EndZ=0
    g5: LineSegment StartX=-33.8 StartY=36.4429 StartZ=0 EndX=-27.6 EndY=30.1929 EndZ=0
  constraints (14):
    c: Coincident(g2,g0)
    c: Coincident(g3,g0)
    c: Coincident(g4,g1)
    c: Coincident(g5,g1)
    c: Equal(g5,g4)
    c: Equal(g4,g2)
    c: Equal(g2,g3)
    c: Equal(g0,g1)
    c: Diameter(g1) = 6.4
    c: Distance(g1,g0) = 15
    c: Coincident(g2,g-4)
    c: Coincident(g4,g-4)
    c: Coincident(g5,g-3)
    c: Coincident(g3,g-3)
FEATURE [PartDesign::Pocket] Pocket
  BaseFeature = -> Pad006
  Length = 5
  Length2 = 100
  Profile = -> Sketch012
  Type = 0
FEATURE [PartDesign::Pad] Pad010
  BaseFeature = -> Pocket
  Direction = (1,1,1)
  Length = 78
  Length2 = 100
  Profile = -> Pocket [Face35]
  Type = 0
FEATURE [Sketcher::SketchObject] Sketch013
  ExternalGeometry = -> [Pad010]
  FullyConstrained = false
  MapMode = 5
  Placement = pos=(0,0,0) rot=(1,0,0;1.5708rad)
  Support = -> [XZ_Plane]
  sketch-geometry (5):
    g0: LineSegment StartX=-22.6 StartY=-41.1224 StartZ=0 EndX=53.4896 EndY=-41.1224 EndZ=0
    g1: LineSegment StartX=-22.6 StartY=-28.3642 StartZ=0 EndX=50.3995 EndY=-12.2042 EndZ=0
    g2: LineSegment StartX=50.3995 StartY=-12.2042 StartZ=0 EndX=53.4896 EndY=-12.2042 EndZ=0
    g3: LineSegment StartX=53.4896 StartY=-12.2042 StartZ=0 EndX=53.4896 EndY=-41.1224 EndZ=0
    g4: LineSegment StartX=-22.6 StartY=-28.3642 StartZ=0 EndX=-22.6 EndY=-41.1224 EndZ=0
  constraints (12):
    c: Horizontal(g0)
    c: Coincident(g2,g1)
    c: Horizontal(g2)
    c: Coincident(g3,g2)
    c: Coincident(g3,g0)
    c: Vertical(g3)
    c: Coincident(g4,g1)
    c: Coincident(g4,g0)
    c: Vertical(g4)
    c: PointOnObject(g1,g-4)
    c: Distance(g1,g-4) = 5
    c: Coincident(g1,g-3)
FEATURE [PartDesign::Pocket] Pocket001
  BaseFeature = -> Pad010
  Length = 5
  Length2 = 100
  Profile = -> Sketch013
  Type = 1
FEATURE [Sketcher::SketchObject] Sketch014
  ExternalGeometry = -> [Pocket001]
  FullyConstrained = false
  MapMode = 5
  Placement = pos=(50.3995,0,0) rot=(0.57735,0.57735,0.57735;2.0944rad)
  Support = -> [Pocket001]
  sketch-geometry (4):
    g0: LineSegment StartX=75.2478 StartY=103.35 StartZ=0 EndX=114.419 EndY=78.4245 EndZ=0
    g1: LineSegment StartX=75.2478 StartY=103.35 StartZ=0 EndX=58.9644 EndY=77.7611 EndZ=0
    g2: LineSegment StartX=58.9644 StartY=77.7611 StartZ=0 EndX=29.0813 EndY=-10.1793 EndZ=0
    g3: LineSegment StartX=29.0813 StartY=-10.1793 StartZ=0 EndX=114.419 EndY=78.4245 EndZ=0
  constraints (10):
    c: PointOnObject(g0,g-3)
    c: Distance(g0,g-3) = 8
    c: PointOnObject(g-3,g0)
    c: Coincident(g1,g0)
    c: PointOnObject(g1,g-4)
    c: Perpendicular(g-3,g1)
    c: Coincident(g2,g1)
    c: Coincident(g2,g-5)
    c: Coincident(g3,g2)
    c: Coincident(g3,g0)
FEATURE [Sketcher::SketchObject] Sketch015
  FullyConstrained = false
  MapMode = 5
  Placement = pos=(0,-9e-15,5.7e-15) rot=(0,0.876601,0.481218;3.14159rad)
  Support = -> [Pocket001]
  sketch-geometry (6):
    g0: LineSegment StartX=-47.9995 StartY=127.591 StartZ=0 EndX=57.4 EndY=127.591 EndZ=0
    g1: LineSegment StartX=55 StartY=125.191 StartZ=0 EndX=-47.9995 EndY=125.191 EndZ=0
    g2: LineSegment StartX=-47.9995 StartY=125.191 StartZ=0 EndX=-47.9995 EndY=127.591 EndZ=0
    g3: LineSegment StartX=57.4 StartY=26.6861 StartZ=0 EndX=55 EndY=26.6861 EndZ=0
    g4: LineSegment StartX=55 StartY=26.6861 StartZ=0 EndX=55 EndY=125.191 EndZ=0
    g5: LineSegment StartX=57.4 StartY=127.591 StartZ=0 EndX=57.4 EndY=26.6861 EndZ=0
  constraints (17):
    c: Coincident(g1,g2)
    c: Coincident(g2,g0)
    c: Horizontal(g0)
    c: Horizontal(g1)
    c: Vertical(g2)
    c: Distance(g2) = 2.4
    c: Coincident(g3,g4)
    c: Coincident(g5,g3)
    c: Horizontal(g3)
    c: Vertical(g4)
    c: Vertical(g5)
    c: Distance(g3) = 2.4
    c: Coincident(g4,g1)
    c: Coincident(g0,g5)
    c: DistanceX(g0) = -47.9995
    c: DistanceY(g0) = 127.591
    c: DistanceX(g1) = 55
FEATURE [PartDesign::Pad] Pad011
  BaseFeature = -> Pocket001
  Direction = (1,1,1)
  Length = 10
  Length2 = 100
  Profile = -> Sketch015
  Type = 3
  UpToFace = -> Pocket001 [Face30]
FEATURE [PartDesign::Pocket] Pocket002
  BaseFeature = -> Pad011
  Length = 0
  Length2 = 100
  Profile = -> Sketch014
  Type = 3
  UpToFace = -> Pad011 [Face35]
FEATURE [Sketcher::SketchObject] Sketch016
  FullyConstrained = false
  MapMode = 5
  Placement = pos=(55,0,0) rot=(0.57735,0.57735,0.57735;2.0944rad)
  sketch-geometry (4):
    g0: LineSegment StartX=0.911414 StartY=0 StartZ=0 EndX=-2.10666 EndY=0 EndZ=0
    g1: LineSegment StartX=-2.10666 StartY=0 StartZ=0 EndX=-2.10666 EndY=1 EndZ=0
    g2: LineSegment StartX=-2.10666 StartY=1 StartZ=0 EndX=0.911414 EndY=1 EndZ=0
    g3: LineSegment StartX=0.911414 StartY=1 StartZ=0 EndX=0.911414 EndY=0 EndZ=0
  constraints (10):
    c: Coincident(g0,g1)
    c: Coincident(g1,g2)
    c: Coincident(g2,g3)
    c: Coincident(g3,g0)
    c: Horizontal(g0)
    c: Horizontal(g2)
    c: Vertical(g1)
    c: Vertical(g3)
    c: PointOnObject(g0,g-1)
    c: Distance(g3) = 1
FEATURE [Sketcher::SketchObject] Sketch017
  FullyConstrained = true
  MapMode = 5
  Support = -> [Pad009]
FEATURE [PartDesign::Body] Body001
  Group = -> [Binder,Sketch004,Pad003,Mirrored001,Sketch005,Pad004,Sketch006,Pad005,Sketch011,Pad009,Sketch017]
  Origin = -> Origin001
  Tip = -> Pad009
FEATURE [Sketcher::SketchObject] Sketch019
  AttachmentOffset = pos=(0,0,-22.7) rot=(0,0,1;0rad)
  FullyConstrained = false
  MapMode = 5
  Placement = pos=(-22.7,5e-15,-5e-15) rot=(0.57735,0.57735,0.57735;2.0944rad)
  Support = -> [YZ_Plane]
  sketch-geometry (3):
    g0: LineSegment StartX=30.1929 StartY=-12.2042 StartZ=0 EndX=42.6929 EndY=-28.3642 EndZ=0
    g1: LineSegment StartX=30.1929 StartY=-12.2042 StartZ=0 EndX=30.1929 EndY=-28.3642 EndZ=0
    g2: LineSegment StartX=30.1929 StartY=-28.3642 StartZ=0 EndX=42.6929 EndY=-28.3642 EndZ=0
  constraints (5):
    c: Coincident(g1,g0)
    c: Vertical(g1)
    c: Coincident(g2,g1)
    c: Coincident(g2,g0)
    c: Horizontal(g2)
FEATURE [PartDesign::Pocket] Pocket003
  BaseFeature = -> Pocket002
  Length = 5
  Length2 = 100
  Profile = -> Pocket002 [Face57]
  Type = 0
FEATURE [Sketcher::SketchObject] Sketch020
  AttachmentOffset = pos=(0,0,-23) rot=(0,0,1;0rad)
  FullyConstrained = false
  MapMode = 5
  Placement = pos=(-23,5.1e-15,-5.1e-15) rot=(0.57735,0.57735,0.57735;2.0944rad)
  Support = -> [YZ_Plane]
  sketch-geometry (4):
    g0: LineSegment StartX=28.0095 StartY=-11.949 StartZ=0 EndX=28.0334 EndY=-32.4386 EndZ=0
    g1: LineSegment StartX=0 StartY=0 StartZ=0 EndX=28.0334 EndY=-32.4386 EndZ=0
    g2: LineSegment StartX=28.0095 StartY=-11.949 StartZ=0 EndX=3.49844 EndY=4.21293 EndZ=0
    g3: LineSegment StartX=3.49844 StartY=4.21293 StartZ=0 EndX=0 EndY=0 EndZ=0
  constraints (5):
    c: Coincident(g1,g0)
    c: Coincident(g2,g0)
    c: Coincident(g3,g2)
    c: Coincident(g3,g1)
    c: Coincident(g1,g-1)
FEATURE [PartDesign::Pad] Pad012
  BaseFeature = -> Pocket003
  Direction = (1,1,1)
  Length = 2.4
  Length2 = 100
  Profile = -> Sketch020
  Reversed = true
  Type = 0
FEATURE [Sketcher::SketchObject] Sketch021
  FullyConstrained = false
  MapMode = 5
  Placement = pos=(-55,0,0) rot=(0.57735,0.57735,0.57735;2.0944rad)
  Support = -> [Pad012]
  sketch-geometry (4):
    g0: LineSegment StartX=42.6878 StartY=-28.3787 StartZ=0 EndX=40.4425 EndY=-6.48667 EndZ=0
    g1: LineSegment StartX=42.6878 StartY=-28.3787 StartZ=0 EndX=30.264 EndY=-28.5923 EndZ=0
    g2: LineSegment StartX=40.4425 StartY=-6.48667 StartZ=0 EndX=38.9244 EndY=0.0404295 EndZ=0
    g3: LineSegment StartX=38.9244 StartY=0.0404295 StartZ=0 EndX=30.264 EndY=-28.5923 EndZ=0
  constraints (4):
    c: Coincident(g1,g0)
    c: Coincident(g2,g0)
    c: Coincident(g3,g2)
    c: Coincident(g3,g1)
FEATURE [PartDesign::Pad] Pad013
  BaseFeature = -> Pad012
  Direction = (1,1,1)
  Length = 2.4
  Length2 = 100
  Profile = -> Sketch021
  Type = 0
FEATURE [PartDesign::Pad] Pad014
  BaseFeature = -> Pad013
  Direction = (1,1,1)
  Length = 2.4
  Length2 = 100
  Profile = -> Sketch019
  Reversed = true
  Type = 0
FEATURE [PartDesign::Pad] Pad017
  BaseFeature = -> Pad014
  Direction = (1,1,1)
  Length = 2.4
  Length2 = 100
  Profile = -> Sketch010
  Reversed = true
  Type = 0
FEATURE [PartDesign::Pocket] Pocket004
  BaseFeature = -> Pad017
  Length = 5
  Length2 = 100
  Profile = -> Pad017 [Face69]
  Type = 0
FEATURE [PartDesign::Pad] Pad018
  BaseFeature = -> Pocket004
  Direction = (1,1,1)
  Length = 1
  Length2 = 100
  Profile = -> Pocket004 [Face49]
  Type = 0
FEATURE [PartDesign::Pad] Pad019
  BaseFeature = -> Pad018
  Direction = (1,1,1)
  Length = 1.5
  Length2 = 100
  Profile = -> Pad018 [Face34]
  Type = 0
FEATURE [PartDesign::Body] Body
  Group = -> [Sketch,Pad,Mirrored,Sketch001,Pad001,Sketch002,Pad002,Sketch003,Sketch007,Pad006,Sketch008,Sketch010,Sketch012,Pocket,Pad010,Sketch013,Pocket001,Sketch014,Sketch015,Pad011,Pocket002,Sketch016,Sketch019,Pocket003,Sketch020,Pad012,Sketch021,Pad013,Pad014,Pad017,Pocket004,Pad018,Pad019]
  Origin = -> Origin
  Tip = -> Pad019
